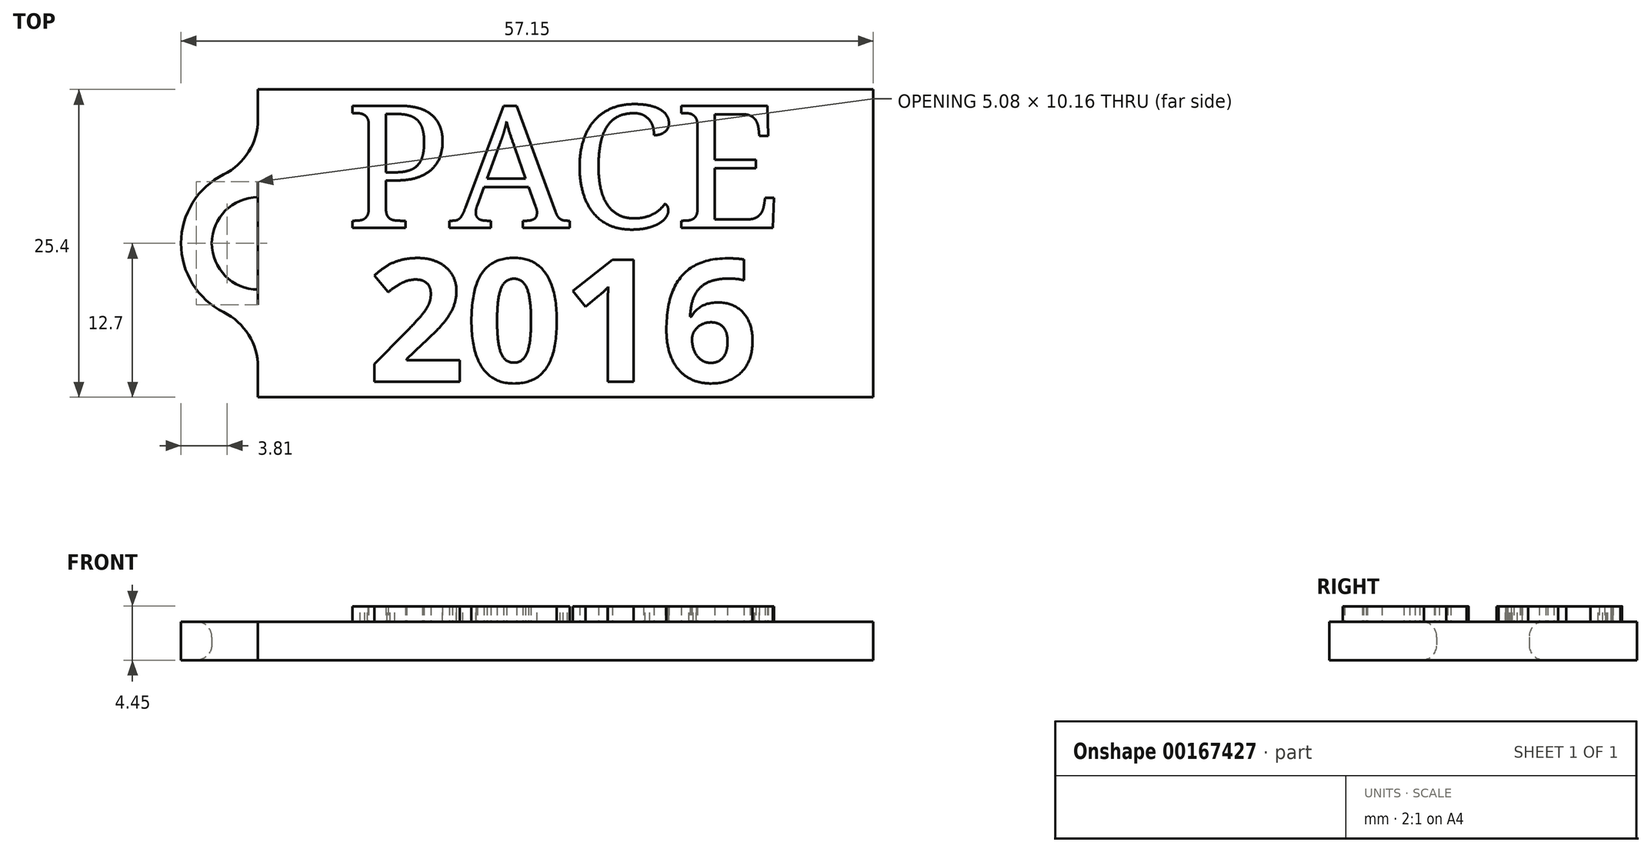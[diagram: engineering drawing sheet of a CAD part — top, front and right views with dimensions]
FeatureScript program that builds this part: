
annotation { "Feature Type Name" : "Feature", "Feature Type Description" : "" }
export const myFeature = defineFeature(function(context is Context, id is Id, definition is map)
    precondition{}
    {
        {
            var Q0;
            Q0=qCreatedBy(makeId("Top.planeOp"),FACE);
            var sketch = newSketch(context, id + "F0", { "sketchPlane" : qUnion([Q0])});
            skLineSegment(sketch, "E0.bottom", {"start": v(0, 0) * mm, "end": v(50.8, 0) * mm});
            skLineSegment(sketch, "E0.top", {"start": v(0, 25.4) * mm, "end": v(50.8, 25.4) * mm});
            skLineSegment(sketch, "E0.left", {"start": v(0, 0) * mm, "end": v(0, 25.4) * mm});
            skLineSegment(sketch, "E0.right", {"start": v(50.8, 0) * mm, "end": v(50.8, 25.4) * mm});
            skLineSegment(sketch, "E1", {"start": v(0, 12.7) * mm, "end": v(-26.85, 12.7) * mm, "construction": true});
            skArc(sketch, "E2", {"start": v(0, 19.05) * mm, "mid": v(-6.35, 12.7) * mm, "end": v(0, 6.35) * mm});
            skArc(sketch, "E3", {"start": v(0, 16.51) * mm, "mid": v(-3.81, 12.7) * mm, "end": v(0, 8.9) * mm});
            skSolve(sketch);
        }
        {
            var Q0;
            {var subQ5=sQuery(id+"F0.wireOp",EDGE,"E0.bottom");Q0=makeQuery(id+"F0.imprint","IMPRINT",FACE,{"disambiguationData":[TD([[makeQuery(id+"F0.imprint","IMPRINT",EDGE,{"derivedFrom":subQ5}),1.0]])]});}
            var Q1;
            {var subQ0=sQuery(id+"F0.wireOp",EDGE,"E2");Q1=makeQuery(id+"F0.imprint","IMPRINT",FACE,{"disambiguationData":[TD([[makeQuery(id+"F0.imprint","IMPRINT",EDGE,{"derivedFrom":subQ0}),1.0]])]});}
            extrude(context, id + "F1", {"entities" : qUnion([Q0, Q1]), "depth" : 3.17 * mm});
        }
        {
            var Q0;
            {var subQ0=sQuery(id+"F0.wireOp",EDGE,"E2");var subQ1=sQuery(id+"F0.wireOp",EDGE,"E0.left");Q0=makeQuery(id+"F1.opExtrude","SWEPT_EDGE",EDGE,{"disambiguationData":[OSD([subQ1,subQ0]),TDD([makeQuery(id+"F0.imprint","INTERSECT",VERTEX,{"disambiguationData":[OD(0.0)],"derivedFrom":[subQ1,subQ0]})])]});}
            var Q1;
            {var subQ0=sQuery(id+"F0.wireOp",EDGE,"E2");var subQ1=sQuery(id+"F0.wireOp",EDGE,"E0.left");Q1=makeQuery(id+"F1.opExtrude","SWEPT_EDGE",EDGE,{"disambiguationData":[OSD([subQ1,subQ0]),TDD([makeQuery(id+"F0.imprint","INTERSECT",VERTEX,{"disambiguationData":[OD(1.0)],"derivedFrom":[subQ1,subQ0]})])]});}
            fillet(context, id + "F2", {"entities" : qUnion([Q0, Q1]), "radius" : 5.08 * mm, "tangentPropagation" : true, "allowEdgeOverflow" : false});
        }
        {
            var Q0;
            Q0=makeQuery(id+"F1.opExtrude","CAP_EDGE",EDGE,{"disambiguationData":[OSD([sQuery(id+"F0.wireOp",EDGE,"E3")])],"isStart":false});
            var Q1;
            Q1=makeQuery(id+"F1.opExtrude","CAP_EDGE",EDGE,{"disambiguationData":[OSD([sQuery(id+"F0.wireOp",EDGE,"E3")])],"isStart":true});
            fillet(context, id + "F3", {"entities" : qUnion([Q0, Q1]), "radius" : 1.27 * mm, "tangentPropagation" : true, "allowEdgeOverflow" : false});
        }
        {
            var Q0;
            Q0=makeQuery(id+"F1.opExtrude","CAP_FACE",FACE,{"disambiguationData":[OSD([sQuery(id+"F0.wireOp",EDGE,"E0.bottom"),sQuery(id+"F0.wireOp",EDGE,"E0.top"),sQuery(id+"F0.wireOp",EDGE,"E0.left"),sQuery(id+"F0.wireOp",EDGE,"E0.right"),sQuery(id+"F0.wireOp",EDGE,"E2"),sQuery(id+"F0.wireOp",EDGE,"E3")])],"isStart":false});
            var sketch = newSketch(context, id + "F4", { "sketchPlane" : qUnion([Q0])});
            skText(sketch, "E4", { "text": "PACE", "fontName": "NotoSerif-Regular.ttf"});
            skLineSegment(sketch, "E5", {"start": v(25.4, 25.4) * mm, "end": v(25.4, 0) * mm, "construction": true});
            skLineSegment(sketch, "E6", {"start": v(50.8, 12.7) * mm, "end": v(0, 12.7) * mm, "construction": true});
            skText(sketch, "E7", { "text": "2016", "fontName": "OpenSans-Bold.ttf"});
            const initialGuessF4  = {"E4": [0.00727, 0.01397, 1, 0, 0.01016], "E7": [0.00906, 0.00127, 1, 0, 0.01016]};
            skSetInitialGuess(sketch, initialGuessF4);
            skSolve(sketch);
        }
        {
            var Q0;
            Q0 = qSketchRegion(id + "F4", true);
            extrude(context, id + "F5", {"entities" : qUnion([Q0]), "operationType" : NewBodyOperationType.ADD, "depth" : 1.27 * mm});
        }
    });
